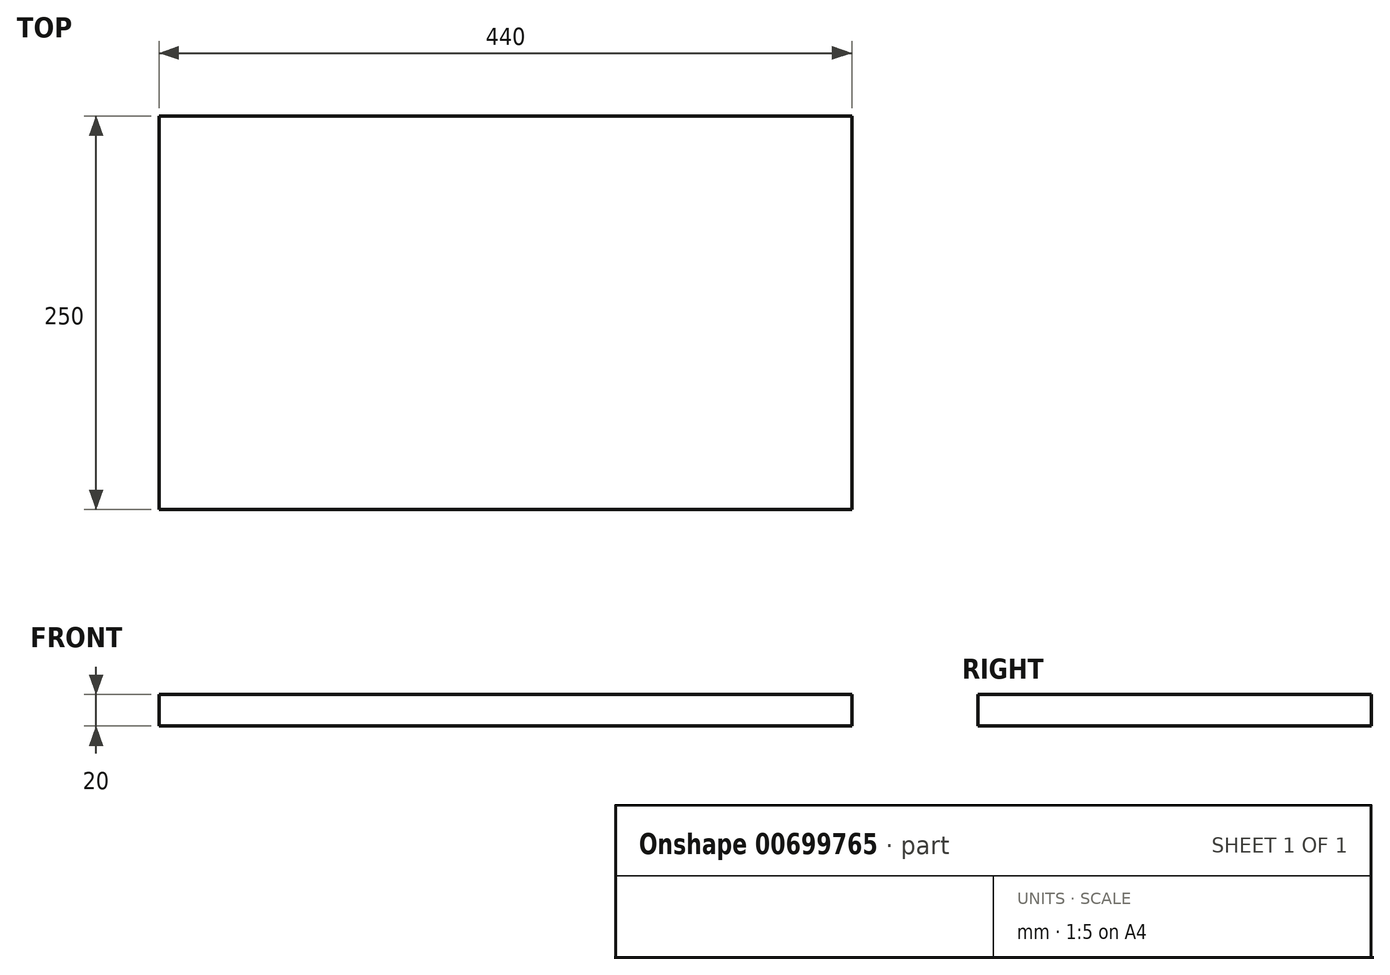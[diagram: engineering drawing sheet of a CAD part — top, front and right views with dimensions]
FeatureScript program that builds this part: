
annotation { "Feature Type Name" : "Feature", "Feature Type Description" : "" }
export const myFeature = defineFeature(function(context is Context, id is Id, definition is map)
    precondition{}
    {
        {
            var Q0;
            Q0=qCreatedBy(makeId("Top.planeOp"),FACE);
            var sketch = newSketch(context, id + "F0", { "sketchPlane" : qUnion([Q0])});
            skLineSegment(sketch, "E0.bottom", {"start": v(220, -125) * mm, "end": v(-220, -125) * mm});
            skLineSegment(sketch, "E0.top", {"start": v(220, 125) * mm, "end": v(-220, 125) * mm});
            skLineSegment(sketch, "E0.left", {"start": v(220, -125) * mm, "end": v(220, 125) * mm});
            skLineSegment(sketch, "E0.right", {"start": v(-220, -125) * mm, "end": v(-220, 125) * mm});
            skPoint(sketch, "E0.middle", {"position": v(0, 0) * mm});
            skSolve(sketch);
        }
        {
            var Q0;
            Q0=makeQuery(id+"F0.imprint","IMPRINT",FACE,{"disambiguationData":[TD([[makeQuery(id+"F0.imprint","IMPRINT",EDGE,{"derivedFrom":sQuery(id+"F0.wireOp",EDGE,"E0.bottom")}),-1.0]])]});
            extrude(context, id + "F1", {"entities" : qUnion([Q0]), "oppositeDirection" : true, "depth" : 20 * mm, "offsetDistance" : 25 * mm});
        }
    });
